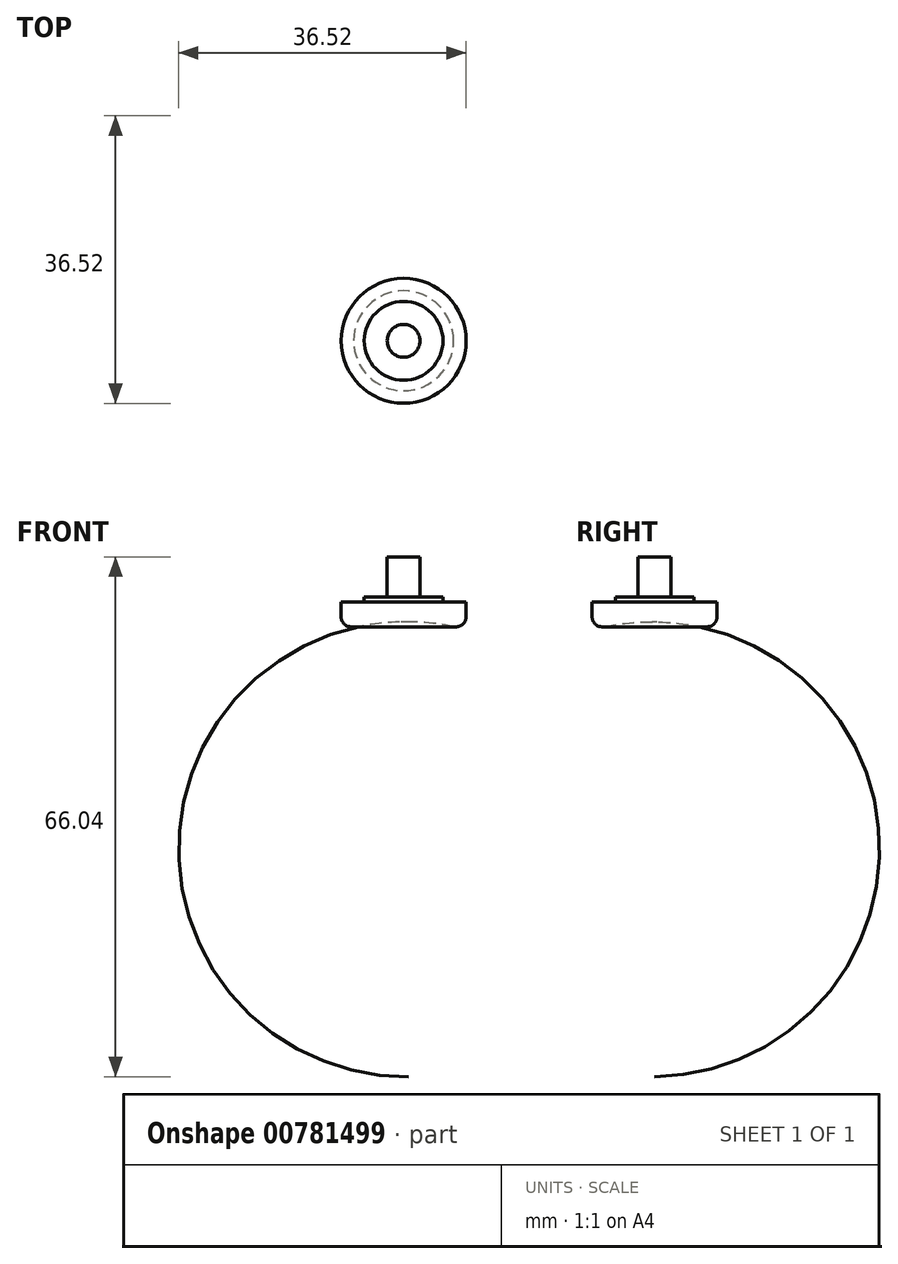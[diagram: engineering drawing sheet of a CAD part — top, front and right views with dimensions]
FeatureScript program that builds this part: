
annotation { "Feature Type Name" : "Feature", "Feature Type Description" : "" }
export const myFeature = defineFeature(function(context is Context, id is Id, definition is map)
    precondition{}
    {
        {
            var Q0;
            Q0=qCreatedBy(makeId("Top.planeOp"),FACE);
            var sketch = newSketch(context, id + "F0", { "sketchPlane" : qUnion([Q0])});
            skCircle(sketch, "E0", {"center": v(0, 0) * mm, "radius": 7.94 * mm});
            skSolve(sketch);
        }
        {
            var Q0;
            Q0=makeQuery(id+"F0.imprint","IMPRINT",FACE,{"disambiguationData":[TD([[makeQuery(id+"F0.imprint","IMPRINT",EDGE,{"derivedFrom":sQuery(id+"F0.wireOp",EDGE,"E0")}),1.0]])]});
            extrude(context, id + "F1", {"entities" : qUnion([Q0]), "depth" : 3.17 * mm, "offsetDistance" : 25.4 * mm});
        }
        {
            var Q0;
            Q0=makeQuery(id+"F1.opExtrude","CAP_FACE",FACE,{"disambiguationData":[OSD([sQuery(id+"F0.wireOp",EDGE,"E0")])],"isStart":false});
            var sketch = newSketch(context, id + "F2", { "sketchPlane" : qUnion([Q0])});
            skCircle(sketch, "E1", {"center": v(0, 0) * mm, "radius": 3 * mm});
            skSolve(sketch);
        }
        {
            var Q0;
            Q0=makeQuery(id+"F1.opExtrude","CAP_EDGE",EDGE,{"disambiguationData":[OSD([sQuery(id+"F0.wireOp",EDGE,"E0")])],"isStart":true});
            fillet(context, id + "F3", {"entities" : qUnion([Q0]), "radius" : 1.27 * mm, "tangentPropagation" : true, "allowEdgeOverflow" : false});
        }
        {
            var Q0;
            Q0=qCreatedBy(makeId("Front.planeOp"),FACE);
            var sketch = newSketch(context, id + "F4", { "sketchPlane" : qUnion([Q0])});
            skLineSegment(sketch, "E2", {"start": v(0, 0) * mm, "end": v(0, 0.64) * mm});
            skLineSegment(sketch, "E3", {"start": v(6.35, 0) * mm, "end": v(0, 0) * mm});
            skLineSegment(sketch, "E4", {"start": v(0, 0.64) * mm, "end": v(0.64, 0.64) * mm});
            skArc(sketch, "E5", {"start": v(6.35, 0) * mm, "mid": v(3.2, 0.5) * mm, "end": v(0, 0.64) * mm});
            skSolve(sketch);
        }
        {
            var Q0;
            Q0=qCreatedBy(makeId("Front.planeOp"),FACE);
            var sketch = newSketch(context, id + "F5", { "sketchPlane" : qUnion([Q0])});
            skLineSegment(sketch, "E6", {"start": v(0, 0) * mm, "end": v(0, 17.2) * mm, "construction": true});
            skSolve(sketch);
        }
        {
            var Q0;
            Q0=qSketchRegion(id+"F4",true);
            var Q1;
            Q1=sQuery(id+"F5.wireOp",EDGE,"E6");
            revolve(context, id + "F6", {"operationType" : NewBodyOperationType.REMOVE, "surfaceOperationType" : NewSurfaceOperationType.NEW, "entities" : qUnion([Q0]), "axis" : qUnion([Q1]), "revolveType" : RevolveType.FULL, "oppositeDirection" : true});
        }
        {
            var Q0;
            Q0=makeQuery(id+"F1.opExtrude","CAP_FACE",FACE,{"disambiguationData":[OSD([sQuery(id+"F0.wireOp",EDGE,"E0")])],"isStart":false});
            var sketch = newSketch(context, id + "F7", { "sketchPlane" : qUnion([Q0])});
            skCircle(sketch, "E7", {"center": v(0, 0) * mm, "radius": 5 * mm});
            skCircle(sketch, "E8", {"center": v(0, 0) * mm, "radius": 2.08 * mm});
            skSolve(sketch);
        }
        {
            var Q0;
            Q0=makeQuery(id+"F7.imprint","IMPRINT",FACE,{"disambiguationData":[TD([[makeQuery(id+"F7.imprint","IMPRINT",EDGE,{"derivedFrom":sQuery(id+"F7.wireOp",EDGE,"E7")}),1.0]])]});
            extrude(context, id + "F8", {"entities" : qUnion([Q0]), "operationType" : NewBodyOperationType.ADD, "depth" : 0.64 * mm, "offsetDistance" : 25.4 * mm});
        }
        {
            var Q0;
            Q0=makeQuery(id+"F2.imprint","IMPRINT",FACE,{"disambiguationData":[TD([[makeQuery(id+"F2.imprint","IMPRINT",EDGE,{"derivedFrom":sQuery(id+"F2.wireOp",EDGE,"E1")}),1.0]])]});
            var sketch = newSketch(context, id + "F9", { "sketchPlane" : qUnion([Q0])});
            skCircle(sketch, "E9", {"center": v(0, 0) * mm, "radius": 2.08 * mm});
            skSolve(sketch);
        }
        {
            var Q0;
            Q0 = qSketchRegion(id + "F9", true);
            extrude(context, id + "F10", {"entities" : qUnion([Q0]), "operationType" : NewBodyOperationType.ADD, "depth" : 5.7 * mm, "offsetDistance" : 25.4 * mm});
        }
    });
